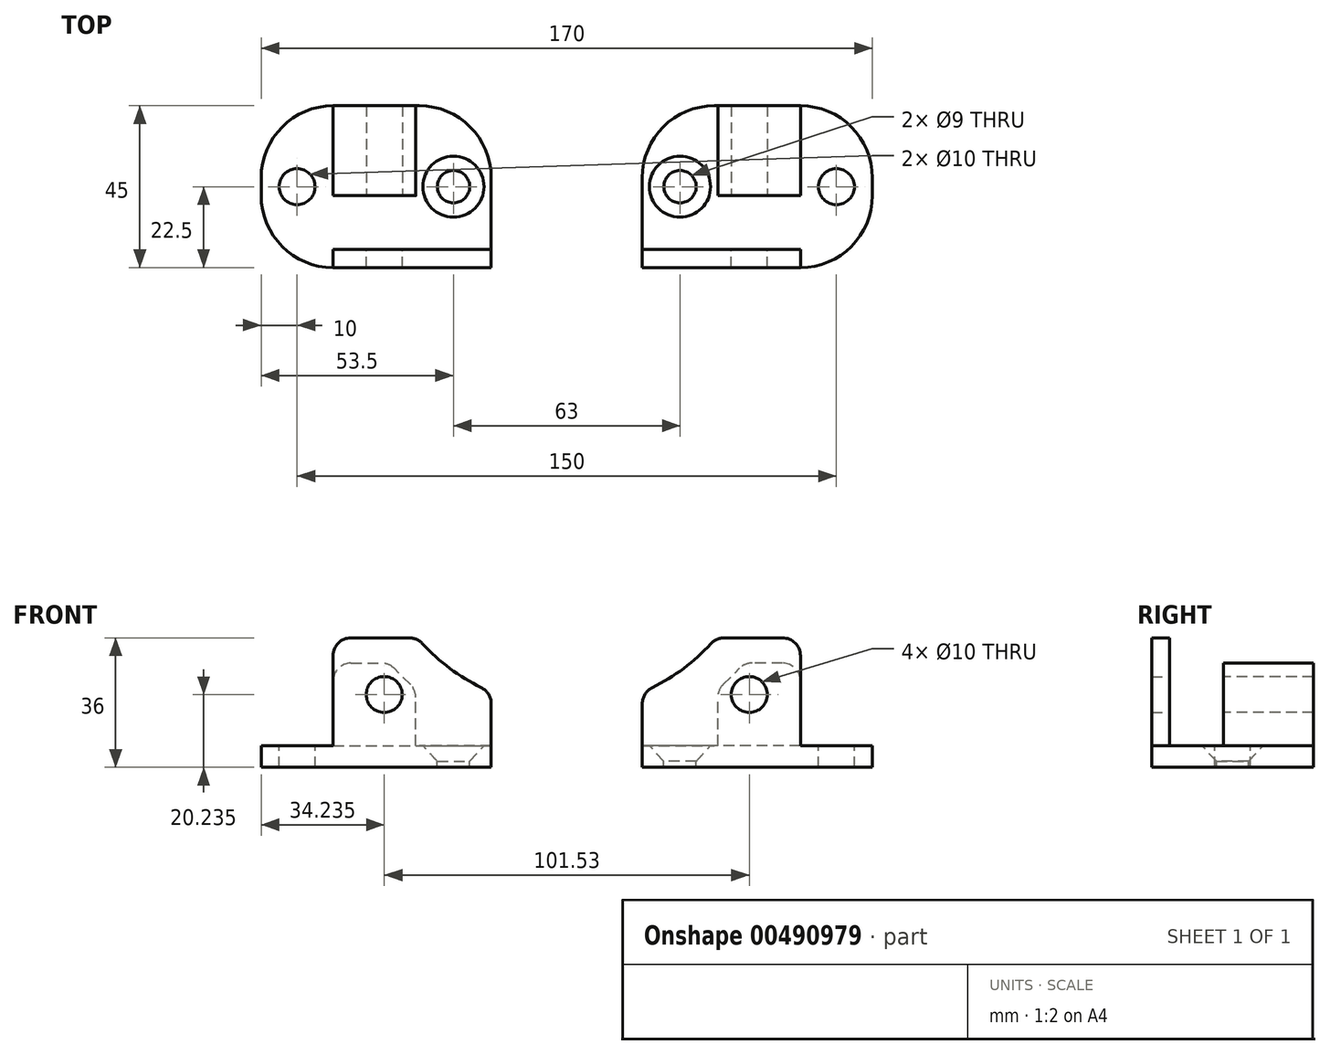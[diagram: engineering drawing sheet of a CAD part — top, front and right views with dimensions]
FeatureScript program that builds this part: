
annotation { "Feature Type Name" : "Feature", "Feature Type Description" : "" }
export const myFeature = defineFeature(function(context is Context, id is Id, definition is map)
    precondition{}
    {
        {
            var Q0;
            Q0=qCreatedBy(makeId("Front.planeOp"),FACE);
            cPlane(context, id + "F0", {"entities" : qUnion([Q0]), "cplaneType" : CPlaneType.OFFSET, "offset" : 15 * mm, "oppositeDirection" : true, "width" : 150 * mm, "height" : 150 * mm});
        }
        {
            var Q0;
            Q0=qCreatedBy(makeId("Top.planeOp"),FACE);
            cPlane(context, id + "F1", {"entities" : qUnion([Q0]), "cplaneType" : CPlaneType.OFFSET, "offset" : 6 * mm, "width" : 150 * mm, "height" : 150 * mm});
        }
        {
            var Q0;
            Q0=qCreatedBy(makeId("Front.planeOp"),FACE);
            var sketch = newSketch(context, id + "F2", { "sketchPlane" : qUnion([Q0])});
            skLineSegment(sketch, "E0", {"start": v(-131, 137) * mm, "end": v(0, 137) * mm});
            skLineSegment(sketch, "E1", {"start": v(-131, 6) * mm, "end": v(0, 6) * mm});
            skCircle(sketch, "E2", {"center": v(-65.5, 71.5) * mm, "radius": 55 * mm});
            skCircle(sketch, "E3", {"center": v(-14.23, 20.23) * mm, "radius": 5 * mm});
            skLineSegment(sketch, "E4", {"start": v(-131, 137) * mm, "end": v(-131, 6) * mm});
            skLineSegment(sketch, "E5", {"start": v(0, 137) * mm, "end": v(0, 6) * mm});
            skSolve(sketch);
        }
        {
            var Q0;
            Q0=qCreatedBy(makeId("Front.planeOp"),FACE);
            var sketch = newSketch(context, id + "F3", { "sketchPlane" : qUnion([Q0])});
            skLineSegment(sketch, "E6", {"start": v(0, 0) * mm, "end": v(-44, 0) * mm});
            skLineSegment(sketch, "E7", {"start": v(0, 0) * mm, "end": v(20, 0) * mm});
            skLineSegment(sketch, "E8", {"start": v(20, 0) * mm, "end": v(20, 6) * mm});
            skLineSegment(sketch, "E9", {"start": v(20, 6) * mm, "end": v(-44, 6) * mm});
            skLineSegment(sketch, "E10", {"start": v(-44, 6) * mm, "end": v(-44, 0) * mm});
            skPoint(sketch, "E11", {"position": v(-65.5, 71.5) * mm});
            skLineSegment(sketch, "E12", {"start": v(-44, 6) * mm, "end": v(-44, 20.88) * mm});
            skPoint(sketch, "E13", {"position": v(0, 6) * mm});
            skLineSegment(sketch, "E14", {"start": v(0, 6) * mm, "end": v(0, 36) * mm});
            skLineSegment(sketch, "E15", {"start": v(0, 36) * mm, "end": v(-23.5, 36) * mm});
            skArc(sketch, "E16", {"start": v(-23.5, 36) * mm, "mid": v(-32.86, 27.23) * mm, "end": v(-44, 20.88) * mm});
            skCircle(sketch, "E17", {"center": v(-14.23, 20.23) * mm, "radius": 5 * mm});
            skSolve(sketch);
        }
        {
            var Q0;
            Q0=qCreatedBy(id+"F0.planeOp",FACE);
            var sketch = newSketch(context, id + "F4", { "sketchPlane" : qUnion([Q0])});
            skPoint(sketch, "E18", {"position": v(0, 6) * mm});
            skLineSegment(sketch, "E19", {"start": v(0, 6) * mm, "end": v(0, 29) * mm});
            skLineSegment(sketch, "E20", {"start": v(0, 29) * mm, "end": v(-15.5, 29) * mm});
            skLineSegment(sketch, "E21", {"start": v(0, 6) * mm, "end": v(-23, 6) * mm});
            skLineSegment(sketch, "E22", {"start": v(-23, 6) * mm, "end": v(-23, 21.5) * mm});
            skLineSegment(sketch, "E23", {"start": v(-23, 21.5) * mm, "end": v(-15.5, 29) * mm});
            skCircle(sketch, "E24", {"center": v(-14.23, 20.23) * mm, "radius": 5 * mm});
            skSolve(sketch);
        }
        {
            var Q0;
            Q0=qCreatedBy(id+"F1.planeOp",FACE);
            var sketch = newSketch(context, id + "F5", { "sketchPlane" : qUnion([Q0])});
            skPoint(sketch, "E25", {"position": v(-44, 0) * mm});
            skLineSegment(sketch, "E26", {"start": v(-44, -5) * mm, "end": v(20, -5) * mm});
            skLineSegment(sketch, "E27", {"start": v(-44, 40) * mm, "end": v(20, 40) * mm});
            skLineSegment(sketch, "E28", {"start": v(-44, 40) * mm, "end": v(-44, -5) * mm});
            skLineSegment(sketch, "E29", {"start": v(20, 40) * mm, "end": v(20, -5) * mm});
            skPoint(sketch, "E30", {"position": v(-23, 15) * mm});
            skPoint(sketch, "E31", {"position": v(0, 15) * mm});
            skPoint(sketch, "E32", {"position": v(-33.5, 15) * mm});
            skPoint(sketch, "E33", {"position": v(10, 15) * mm});
            skLineSegment(sketch, "E34", {"start": v(-33.5, 15) * mm, "end": v(-33.5, 20) * mm});
            skLineSegment(sketch, "E35", {"start": v(10, 15) * mm, "end": v(10, 20) * mm});
            skPoint(sketch, "E36", {"position": v(-33.5, 17.5) * mm});
            skPoint(sketch, "E37", {"position": v(10, 17.5) * mm});
            skSolve(sketch);
        }
        {
            var Q0;
            Q0=makeQuery(id+"F3.imprint","IMPRINT",FACE,{"disambiguationData":[TD([[makeQuery(id+"F3.imprint","IMPRINT",EDGE,{"derivedFrom":sQuery(id+"F3.wireOp",EDGE,"E6")}),-1.0]])]});
            var Q1;
            {var subQ1=sQuery(id+"F3.wireOp",EDGE,"E12");Q1=makeQuery(id+"F3.imprint","IMPRINT",FACE,{"disambiguationData":[TD([[makeQuery(id+"F3.imprint","IMPRINT",EDGE,{"derivedFrom":subQ1}),-1.0]])]});}
            extrude(context, id + "F6", {"entities" : qUnion([Q0, Q1]), "depth" : 5 * mm});
        }
        {
            var Q0;
            Q0=makeQuery(id+"F3.imprint","IMPRINT",FACE,{"disambiguationData":[TD([[makeQuery(id+"F3.imprint","IMPRINT",EDGE,{"derivedFrom":sQuery(id+"F3.wireOp",EDGE,"E6")}),-1.0]])]});
            extrude(context, id + "F7", {"entities" : qUnion([Q0]), "operationType" : NewBodyOperationType.ADD, "oppositeDirection" : true, "depth" : 40 * mm});
        }
        {
            var Q0;
            Q0=makeQuery(id+"F4.imprint","IMPRINT",FACE,{"disambiguationData":[TD([[makeQuery(id+"F4.imprint","IMPRINT",EDGE,{"derivedFrom":sQuery(id+"F4.wireOp",EDGE,"E19")}),1.0]])]});
            extrude(context, id + "F8", {"entities" : qUnion([Q0]), "operationType" : NewBodyOperationType.ADD, "oppositeDirection" : true, "depth" : 25 * mm});
        }
        {
            var Q0;
            Q0=makeQuery(id+"F8.opExtrude","SWEPT_EDGE",EDGE,{"disambiguationData":[OSD([sQuery(id+"F4.wireOp",EDGE,"E20"),sQuery(id+"F4.wireOp",EDGE,"E23")])]});
            var Q1;
            Q1=makeQuery(id+"F8.opExtrude","SWEPT_EDGE",EDGE,{"disambiguationData":[OSD([sQuery(id+"F4.wireOp",EDGE,"E22"),sQuery(id+"F4.wireOp",EDGE,"E23")])]});
            var Q2;
            Q2=makeQuery(id+"F8.opExtrude","SWEPT_EDGE",EDGE,{"disambiguationData":[OSD([sQuery(id+"F4.wireOp",EDGE,"E19"),sQuery(id+"F4.wireOp",EDGE,"E20")])]});
            var Q3;
            Q3=makeQuery(id+"F6.opExtrude","SWEPT_EDGE",EDGE,{"disambiguationData":[OSD([sQuery(id+"F3.wireOp",EDGE,"E15"),sQuery(id+"F3.wireOp",EDGE,"E16")])]});
            var Q4;
            Q4=makeQuery(id+"F6.opExtrude","SWEPT_EDGE",EDGE,{"disambiguationData":[OSD([sQuery(id+"F3.wireOp",EDGE,"E12"),sQuery(id+"F3.wireOp",EDGE,"E16")])]});
            var Q5;
            Q5=makeQuery(id+"F6.opExtrude","SWEPT_EDGE",EDGE,{"disambiguationData":[OSD([sQuery(id+"F3.wireOp",EDGE,"E14"),sQuery(id+"F3.wireOp",EDGE,"E15")])]});
            fillet(context, id + "F9", {"entities" : qUnion([Q0, Q1, Q2, Q3, Q4, Q5]), "radius" : 5 * mm, "tangentPropagation" : true, "allowEdgeOverflow" : false});
        }
        {
            var Q0;
            Q0=makeQuery(id+"F6.opExtrude","CAP_EDGE",EDGE,{"disambiguationData":[OSD([sQuery(id+"F3.wireOp",EDGE,"E8")])],"isStart":false});
            var Q1;
            Q1=makeQuery(id+"F7.opExtrude","CAP_EDGE",EDGE,{"disambiguationData":[OSD([sQuery(id+"F3.wireOp",EDGE,"E8")])],"isStart":false});
            var Q2;
            Q2=makeQuery(id+"F7.opExtrude","CAP_EDGE",EDGE,{"disambiguationData":[OSD([sQuery(id+"F3.wireOp",EDGE,"E10")])],"isStart":false});
            fillet(context, id + "F10", {"entities" : qUnion([Q0, Q1, Q2]), "radius" : 20 * mm, "tangentPropagation" : true, "allowEdgeOverflow" : false});
        }
        {
            var Q0;
            Q0=sQuery(id+"F5.wireOp",VERTEX,"E36");
            var Q1;
            Q1=makeQuery(id+"F6.opExtrude","SWEPT_BODY",BODY,{"disambiguationData":[OSD([sQuery(id+"F3.wireOp",EDGE,"E6"),sQuery(id+"F3.wireOp",EDGE,"E7"),sQuery(id+"F3.wireOp",EDGE,"E8"),sQuery(id+"F3.wireOp",EDGE,"E9"),sQuery(id+"F3.wireOp",EDGE,"E10"),sQuery(id+"F3.wireOp",EDGE,"E12"),sQuery(id+"F3.wireOp",EDGE,"E14"),sQuery(id+"F3.wireOp",EDGE,"E15"),sQuery(id+"F3.wireOp",EDGE,"E16"),sQuery(id+"F3.wireOp",EDGE,"E17")])]});
            hole(context, id + "F11", {"style" : HoleStyle.C_SINK, "endStyle" : HoleEndStyle.BLIND, "holeDiameter" : 9 * mm, "cSinkDiameter" : 17 * mm, "cSinkAngle" : 85.3 * degree, "majorDiameter" : 5 * mm, "holeDepth" : 8 * mm, "isTappedThrough" : true, "tappedDepth" : 12 * mm, "tapClearance" : 3, "locations" : qUnion([Q0]), "scope" : qUnion([Q1])});
        }
        {
            var Q0;
            Q0=sQuery(id+"F5.wireOp",VERTEX,"E37");
            var Q1;
            Q1=makeQuery(id+"F6.opExtrude","SWEPT_BODY",BODY,{"disambiguationData":[OSD([sQuery(id+"F3.wireOp",EDGE,"E6"),sQuery(id+"F3.wireOp",EDGE,"E7"),sQuery(id+"F3.wireOp",EDGE,"E8"),sQuery(id+"F3.wireOp",EDGE,"E9"),sQuery(id+"F3.wireOp",EDGE,"E10"),sQuery(id+"F3.wireOp",EDGE,"E12"),sQuery(id+"F3.wireOp",EDGE,"E14"),sQuery(id+"F3.wireOp",EDGE,"E15"),sQuery(id+"F3.wireOp",EDGE,"E16"),sQuery(id+"F3.wireOp",EDGE,"E17")])]});
            hole(context, id + "F12", {"style" : HoleStyle.SIMPLE, "endStyle" : HoleEndStyle.BLIND, "holeDiameter" : 10 * mm, "holeDepth" : 8 * mm, "isTappedThrough" : true, "tappedDepth" : 12 * mm, "tapClearance" : 3, "locations" : qUnion([Q0]), "scope" : qUnion([Q1])});
        }
        {
            var Q0;
            Q0=qCreatedBy(makeId("Right.planeOp"),FACE);
            cPlane(context, id + "F13", {"entities" : qUnion([Q0]), "cplaneType" : CPlaneType.OFFSET, "offset" : 65 * mm, "oppositeDirection" : true, "width" : 150 * mm, "height" : 150 * mm});
        }
        {
            var Q0;
            Q0=makeQuery(id+"F6.opExtrude","SWEPT_BODY",BODY,{"disambiguationData":[OSD([sQuery(id+"F3.wireOp",EDGE,"E6"),sQuery(id+"F3.wireOp",EDGE,"E7"),sQuery(id+"F3.wireOp",EDGE,"E8"),sQuery(id+"F3.wireOp",EDGE,"E9"),sQuery(id+"F3.wireOp",EDGE,"E10"),sQuery(id+"F3.wireOp",EDGE,"E12"),sQuery(id+"F3.wireOp",EDGE,"E14"),sQuery(id+"F3.wireOp",EDGE,"E15"),sQuery(id+"F3.wireOp",EDGE,"E16"),sQuery(id+"F3.wireOp",EDGE,"E17")])]});
            var Q1;
            Q1=qCreatedBy(id+"F13.planeOp",FACE);
            mirror(context, id + "F14", {"entities" : qUnion([Q0]), "mirrorPlane" : qUnion([Q1])});
        }
    });
